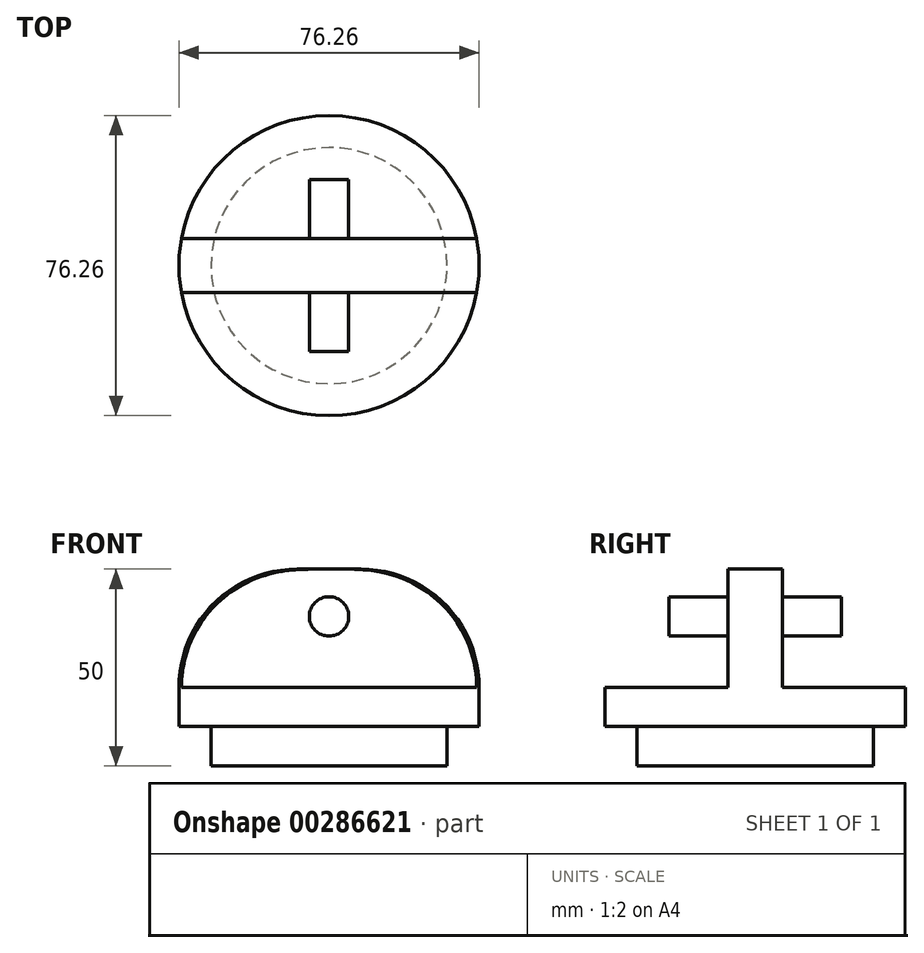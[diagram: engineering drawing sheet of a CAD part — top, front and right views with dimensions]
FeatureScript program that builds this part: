
annotation { "Feature Type Name" : "Feature", "Feature Type Description" : "" }
export const myFeature = defineFeature(function(context is Context, id is Id, definition is map)
    precondition{}
    {
        {
            var Q0;
            Q0=qCreatedBy(makeId("Top.planeOp"),FACE);
            var sketch = newSketch(context, id + "F0", { "sketchPlane" : qUnion([Q0])});
            skCircle(sketch, "E0", {"center": v(0, 0) * mm, "radius": 30 * mm});
            skSolve(sketch);
        }
        {
            var Q0;
            Q0=makeQuery(id+"F0.imprint","IMPRINT",FACE,{"disambiguationData":[TD([[makeQuery(id+"F0.imprint","IMPRINT",EDGE,{"derivedFrom":sQuery(id+"F0.wireOp",EDGE,"E0")}),1.0]])]});
            extrude(context, id + "F1", {"entities" : qUnion([Q0]), "depth" : 10 * mm});
        }
        {
            var Q0;
            Q0=makeQuery(id+"F1.opExtrude","CAP_FACE",FACE,{"disambiguationData":[OSD([sQuery(id+"F0.wireOp",EDGE,"E0")])],"isStart":false});
            var sketch = newSketch(context, id + "F2", { "sketchPlane" : qUnion([Q0])});
            skCircle(sketch, "E1", {"center": v(0, 0) * mm, "radius": 38.13 * mm});
            skSolve(sketch);
        }
        {
            var Q0;
            Q0=makeQuery(id+"F2.imprint","IMPRINT",FACE,{"disambiguationData":[TD([[makeQuery(id+"F2.imprint","IMPRINT",EDGE,{"derivedFrom":makeQuery(id+"F1.opExtrude","CAP_EDGE",EDGE,{"disambiguationData":[OSD([sQuery(id+"F0.wireOp",EDGE,"E0")])],"isStart":false})}),1.0]])]});
            var Q1;
            Q1=makeQuery(id+"F2.imprint","IMPRINT",FACE,{"disambiguationData":[TD([[makeQuery(id+"F2.imprint","IMPRINT",EDGE,{"derivedFrom":sQuery(id+"F2.wireOp",EDGE,"E1")}),1.0]])]});
            extrude(context, id + "F3", {"entities" : qUnion([Q0, Q1]), "operationType" : NewBodyOperationType.ADD, "depth" : 10 * mm});
        }
        {
            var Q0;
            Q0=makeQuery(id+"F3.opExtrude","CAP_FACE",FACE,{"disambiguationData":[OSD([sQuery(id+"F2.wireOp",EDGE,"E1")])],"isStart":false});
            var sketch = newSketch(context, id + "F4", { "sketchPlane" : qUnion([Q0])});
            skLineSegment(sketch, "E2.bottom", {"start": v(-37.5, 6.88) * mm, "end": v(37.5, 6.88) * mm});
            skLineSegment(sketch, "E2.top", {"start": v(-37.5, -6.88) * mm, "end": v(37.5, -6.88) * mm});
            skPoint(sketch, "E2.middle", {"position": v(0, 0) * mm});
            skArc(sketch, "E3", {"start": v(-37.5, -6.88) * mm, "mid": v(-38.13, 0) * mm, "end": v(-37.5, 6.88) * mm});
            skArc(sketch, "E4", {"start": v(37.5, 6.88) * mm, "mid": v(38.13, 0) * mm, "end": v(37.5, -6.88) * mm});
            skSolve(sketch);
        }
        {
            var Q0;
            Q0=makeQuery(id+"F4.imprint","IMPRINT",FACE,{"disambiguationData":[TD([[makeQuery(id+"F4.imprint","IMPRINT",EDGE,{"derivedFrom":sQuery(id+"F4.wireOp",EDGE,"E2.bottom")}),-1.0]])]});
            extrude(context, id + "F5", {"entities" : qUnion([Q0]), "operationType" : NewBodyOperationType.ADD, "depth" : 10 * mm});
        }
        {
            var Q0;
            Q0=makeQuery(id+"F5.opExtrude","CAP_FACE",FACE,{"disambiguationData":[OSD([sQuery(id+"F4.wireOp",EDGE,"E2.bottom"),sQuery(id+"F4.wireOp",EDGE,"E2.top"),sQuery(id+"F4.wireOp",EDGE,"E3"),sQuery(id+"F4.wireOp",EDGE,"E4")])],"isStart":false});
            var sketch = newSketch(context, id + "F6", { "sketchPlane" : qUnion([Q0])});
            skLineSegment(sketch, "E5.bottom", {"start": v(-37.5, 6.88) * mm, "end": v(37.5, 6.88) * mm});
            skLineSegment(sketch, "E5.top", {"start": v(-37.5, -6.88) * mm, "end": v(37.5, -6.88) * mm});
            skPoint(sketch, "E5.middle", {"position": v(0, 0) * mm});
            skArc(sketch, "E6", {"start": v(-37.5, -6.88) * mm, "mid": v(-38.13, 0) * mm, "end": v(-37.5, 6.88) * mm});
            skArc(sketch, "E7", {"start": v(37.5, 6.88) * mm, "mid": v(38.13, 0) * mm, "end": v(37.5, -6.88) * mm});
            skSolve(sketch);
        }
        {
            var Q0;
            Q0 = qSketchRegion(id + "F6", true);
            extrude(context, id + "F7", {"entities" : qUnion([Q0]), "operationType" : NewBodyOperationType.ADD, "depth" : 20 * mm});
        }
        {
            var Q0;
            Q0=makeQuery(id+"F7.opExtrude","CAP_EDGE",EDGE,{"disambiguationData":[OSD([sQuery(id+"F6.wireOp",EDGE,"E7")])],"isStart":false});
            var Q1;
            Q1=makeQuery(id+"F7.opExtrude","CAP_EDGE",EDGE,{"disambiguationData":[OSD([sQuery(id+"F6.wireOp",EDGE,"E6")])],"isStart":false});
            fillet(context, id + "F8", {"entities" : qUnion([Q0, Q1]), "radius" : 30 * mm, "tangentPropagation" : true, "allowEdgeOverflow" : false});
        }
        {
            var Q0;
            Q0=makeQuery(id+"F7.boolean.opBoolean","MERGE",FACE,{"derivedFrom":[makeQuery(id+"F5.opExtrude","SWEPT_FACE",FACE,{"disambiguationData":[OSD([sQuery(id+"F4.wireOp",EDGE,"E2.top")])]}),makeQuery(id+"F7.opExtrude","SWEPT_FACE",FACE,{"disambiguationData":[OSD([sQuery(id+"F6.wireOp",EDGE,"E5.top")])]})]});
            var sketch = newSketch(context, id + "F9", { "sketchPlane" : qUnion([Q0])});
            skCircle(sketch, "E8", {"center": v(0, 38) * mm, "radius": 5 * mm});
            skPoint(sketch, "E8.centerSnap0", {"position": v(0, 50) * mm});
            skSolve(sketch);
        }
        {
            var Q0;
            Q0=makeQuery(id+"F7.boolean.opBoolean","MERGE",FACE,{"derivedFrom":[makeQuery(id+"F5.opExtrude","SWEPT_FACE",FACE,{"disambiguationData":[OSD([sQuery(id+"F4.wireOp",EDGE,"E2.bottom")])]}),makeQuery(id+"F7.opExtrude","SWEPT_FACE",FACE,{"disambiguationData":[OSD([sQuery(id+"F6.wireOp",EDGE,"E5.bottom")])]})]});
            var sketch = newSketch(context, id + "F10", { "sketchPlane" : qUnion([Q0])});
            skCircle(sketch, "E9", {"center": v(0, 38) * mm, "radius": 5 * mm});
            skPoint(sketch, "E9.centerSnap0", {"position": v(0, 50) * mm});
            skSolve(sketch);
        }
        {
            var Q0;
            Q0=makeQuery(id+"F10.imprint","IMPRINT",FACE,{"disambiguationData":[TD([[makeQuery(id+"F10.imprint","IMPRINT",EDGE,{"derivedFrom":sQuery(id+"F10.wireOp",EDGE,"E9")}),1.0]])]});
            extrude(context, id + "F11", {"entities" : qUnion([Q0]), "operationType" : NewBodyOperationType.ADD, "depth" : 15 * mm});
        }
        {
            var Q0;
            Q0=makeQuery(id+"F9.imprint","IMPRINT",FACE,{"disambiguationData":[TD([[makeQuery(id+"F9.imprint","IMPRINT",EDGE,{"derivedFrom":sQuery(id+"F9.wireOp",EDGE,"E8")}),1.0]])]});
            extrude(context, id + "F12", {"entities" : qUnion([Q0]), "operationType" : NewBodyOperationType.ADD, "depth" : 15 * mm});
        }
    });
